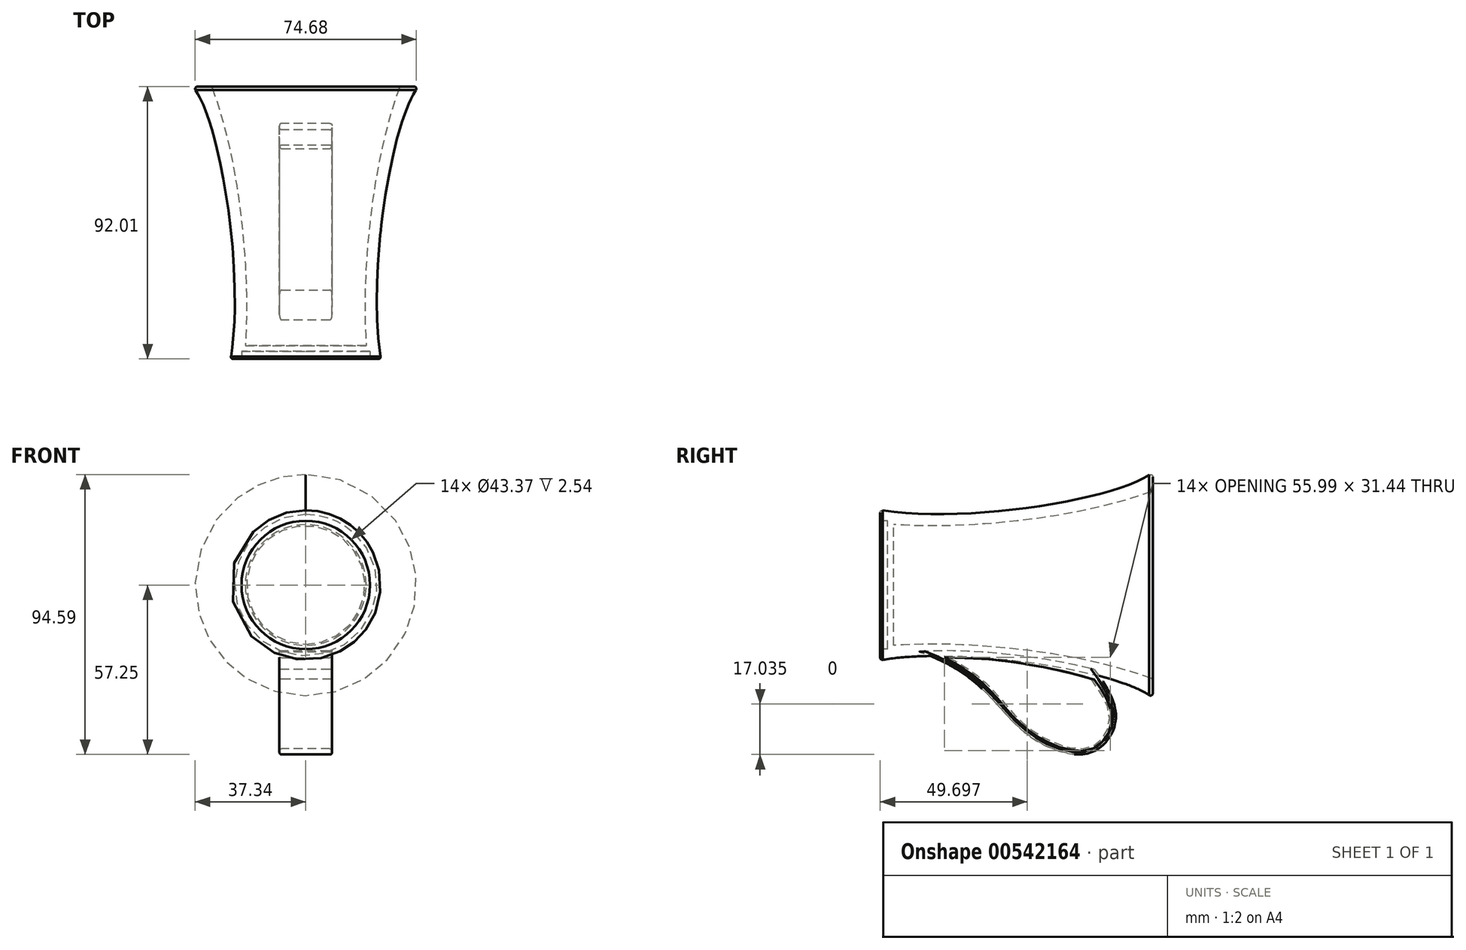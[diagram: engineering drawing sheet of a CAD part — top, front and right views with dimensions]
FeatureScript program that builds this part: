
annotation { "Feature Type Name" : "Feature", "Feature Type Description" : "" }
export const myFeature = defineFeature(function(context is Context, id is Id, definition is map)
    precondition{}
    {
        {
            var Q0;
            Q0=qCreatedBy(makeId("Top.planeOp"),FACE);
            var sketch = newSketch(context, id + "F0", { "sketchPlane" : qUnion([Q0])});
            skLineSegment(sketch, "E0", {"start": v(0, -41.4) * mm, "end": v(25.4, -41.4) * mm});
            skLineSegment(sketch, "E1", {"start": v(0, 50.6) * mm, "end": v(38.1, 50.6) * mm});
            skFitSpline(sketch, "E2", {"points": [v(38.1, 50.6) * mm, v(25.4, -41.4) * mm], "startDerivative": vector(-27.2, -32.14) * mm, "endDerivative": vector(14.87, -86.25) * mm});
            skLineSegment(sketch, "E3", {"start": v(0, 50.6) * mm, "end": v(0, -41.4) * mm});
            skSolve(sketch);
        }
        {
            var Q0;
            Q0 = qSketchRegion(id + "F0", true);
            var Q1;
            Q1=sQuery(id+"F0.wireOp",EDGE,"E3");
            revolve(context, id + "F1", {"entities" : qUnion([Q0]), "axis" : qUnion([Q1]), "revolveType" : RevolveType.FULL});
        }
        {
            var Q0;
            Q0=qCreatedBy(makeId("Top.planeOp"),FACE);
            var sketch = newSketch(context, id + "F2", { "sketchPlane" : qUnion([Q0])});
            skLineSegment(sketch, "E4", {"start": v(0, -36.85) * mm, "end": v(20.4, -36.85) * mm});
            skLineSegment(sketch, "E5", {"start": v(0, 55.37) * mm, "end": v(33.64, 55.37) * mm});
            skFitSpline(sketch, "E6", {"points": [v(33.64, 55.37) * mm, v(21.16, 0) * mm, v(20.4, -36.85) * mm], "startDerivative": vector(-40.95, -98.28) * mm, "endDerivative": vector(5.08, -78.76) * mm});
            skLineSegment(sketch, "E7", {"start": v(0, 55.37) * mm, "end": v(0, -36.85) * mm});
            skSolve(sketch);
        }
        {
            var Q0;
            Q0=makeQuery(id+"F2.imprint","IMPRINT",FACE,{"disambiguationData":[TD([[makeQuery(id+"F2.imprint","IMPRINT",EDGE,{"derivedFrom":sQuery(id+"F2.wireOp",EDGE,"E4")}),1.0]])]});
            var Q1;
            Q1=sQuery(id+"F2.wireOp",EDGE,"E7");
            revolve(context, id + "F3", {"operationType" : NewBodyOperationType.REMOVE, "entities" : qUnion([Q0]), "axis" : qUnion([Q1]), "revolveType" : RevolveType.FULL, "oppositeDirection" : true});
        }
        {
            var Q0;
            Q0=qCreatedBy(makeId("Right.planeOp"),FACE);
            var sketch = newSketch(context, id + "F4", { "sketchPlane" : qUnion([Q0])});
            skFitSpline(sketch, "E8", {"points": [v(30.84, -28.48) * mm, v(37.82, -47.26) * mm, v(29, -56.82) * mm, v(8.9, -50.94) * mm, v(-7.03, -35) * mm, v(-28.21, -22.6) * mm], "startDerivative": vector(93.3, -124.4) * mm, "endDerivative": vector(-113.4, 37.53) * mm});
            skFitSpline(sketch, "E9", {"points": [v(30.84, -28.48) * mm, v(0, -23.26) * mm, v(-28.21, -22.6) * mm], "startDerivative": vector(-67.42, 16.21) * mm, "endDerivative": vector(-57.3, -5) * mm});
            skSolve(sketch);
        }
        {
            var Q0;
            Q0 = qSketchRegion(id + "F4", true);
            extrude(context, id + "F5", {"entities" : qUnion([Q0]), "endBound" : BoundingType.SYMMETRIC, "depth" : 17.78 * mm, "offsetDistance" : 25.4 * mm});
        }
        {
            var Q0;
            Q0=makeQuery(id+"F5.opExtrude","CAP_FACE",FACE,{"disambiguationData":[OSD([sQuery(id+"F4.wireOp",EDGE,"E8"),sQuery(id+"F4.wireOp",EDGE,"E9")])],"isStart":false});
            var sketch = newSketch(context, id + "F6", { "sketchPlane" : qUnion([Q0])});
            skFitSpline(sketch, "E10", {"points": [v(29.68, -31.62) * mm, v(8.76, -26.89) * mm, v(-18.07, -24.52) * mm], "startDerivative": vector(-65.8, 18.8) * mm, "endDerivative": vector(-81.13, 1.2) * mm});
            skFitSpline(sketch, "E11", {"points": [v(29.68, -31.62) * mm, v(36, -44.25) * mm, v(29.68, -54.7) * mm, v(10.34, -49.38) * mm, v(-1.5, -37.54) * mm, v(-18.07, -24.52) * mm], "startDerivative": vector(41.3, -59.3) * mm, "endDerivative": vector(-115.82, 63.17) * mm});
            skSolve(sketch);
        }
        {
            var Q0;
            Q0=makeQuery(id+"F6.imprint","IMPRINT",FACE,{"disambiguationData":[TD([[makeQuery(id+"F6.imprint","IMPRINT",EDGE,{"derivedFrom":sQuery(id+"F6.wireOp",EDGE,"E10")}),1.0]])]});
            extrude(context, id + "F7", {"entities" : qUnion([Q0]), "operationType" : NewBodyOperationType.REMOVE, "endBound" : BoundingType.SYMMETRIC, "oppositeDirection" : true, "depth" : 43.69 * mm, "offsetDistance" : 25.4 * mm});
        }
        {
            var Q0;
            Q0=makeQuery(id+"F1.opRevolve","SWEPT_FACE",FACE,{"disambiguationData":[OSD([sQuery(id+"F0.wireOp",EDGE,"E0")])]});
            var sketch = newSketch(context, id + "F8", { "sketchPlane" : qUnion([Q0])});
            skCircle(sketch, "E12", {"center": v(0, 0) * mm, "radius": 21.69 * mm});
            skSolve(sketch);
        }
        {
            var Q0;
            Q0=makeQuery(id+"F8.imprint","IMPRINT",FACE,{"disambiguationData":[TD([[makeQuery(id+"F8.imprint","IMPRINT",EDGE,{"derivedFrom":sQuery(id+"F8.wireOp",EDGE,"E12")}),1.0]])]});
            extrude(context, id + "F9", {"entities" : qUnion([Q0]), "operationType" : NewBodyOperationType.REMOVE, "oppositeDirection" : true, "depth" : 2.54 * mm, "offsetDistance" : 25.4 * mm});
        }
        {
            var Q0;
            Q0=makeQuery(id+"F1.opRevolve","SWEPT_EDGE",EDGE,{"disambiguationData":[OSD([sQuery(id+"F0.wireOp",EDGE,"E0"),sQuery(id+"F0.wireOp",EDGE,"E2")])]});
            var Q1;
            Q1=makeQuery(id+"F9.boolean.opBoolean","COPY",EDGE,{"derivedFrom":makeQuery(id+"F9.opExtrude","CAP_EDGE",EDGE,{"disambiguationData":[OSD([sQuery(id+"F8.wireOp",EDGE,"E12")])],"isStart":true})});
            var Q2;
            Q2=makeQuery(id+"F5.opExtrude","CAP_EDGE",EDGE,{"disambiguationData":[OSD([sQuery(id+"F4.wireOp",EDGE,"E8")])],"isStart":true});
            var Q3;
            Q3=makeQuery(id+"F7.boolean.opBoolean","INTERSECT",EDGE,{"derivedFrom":[makeQuery(id+"F5.opExtrude","CAP_FACE",FACE,{"disambiguationData":[OSD([sQuery(id+"F4.wireOp",EDGE,"E8"),sQuery(id+"F4.wireOp",EDGE,"E9")])],"isStart":true}),makeQuery(id+"F7.opExtrude","SWEPT_FACE",FACE,{"disambiguationData":[OSD([sQuery(id+"F6.wireOp",EDGE,"E11")])]})]});
            var Q4;
            Q4=makeQuery(id+"F5.opExtrude","CAP_EDGE",EDGE,{"disambiguationData":[OSD([sQuery(id+"F4.wireOp",EDGE,"E8")])],"isStart":false});
            var Q5;
            Q5=makeQuery(id+"F7.boolean.opBoolean","INTERSECT",EDGE,{"derivedFrom":[makeQuery(id+"F5.opExtrude","CAP_FACE",FACE,{"disambiguationData":[OSD([sQuery(id+"F4.wireOp",EDGE,"E8"),sQuery(id+"F4.wireOp",EDGE,"E9")])],"isStart":false}),makeQuery(id+"F7.opExtrude","SWEPT_FACE",FACE,{"disambiguationData":[OSD([sQuery(id+"F6.wireOp",EDGE,"E11")])]})]});
            var Q6;
            Q6=makeQuery(id+"F1.opRevolve","SWEPT_EDGE",EDGE,{"disambiguationData":[OSD([sQuery(id+"F0.wireOp",EDGE,"E1"),sQuery(id+"F0.wireOp",EDGE,"E2")])]});
            var Q7;
            Q7=makeQuery(id+"F3.boolean.opBoolean","INTERSECT",EDGE,{"derivedFrom":[makeQuery(id+"F1.opRevolve","SWEPT_FACE",FACE,{"disambiguationData":[OSD([sQuery(id+"F0.wireOp",EDGE,"E1")])]}),makeQuery(id+"F3.opRevolve","SWEPT_FACE",FACE,{"disambiguationData":[OSD([sQuery(id+"F2.wireOp",EDGE,"E6")])]})]});
            fillet(context, id + "F10", {"entities" : qUnion([Q0, Q1, Q2, Q3, Q4, Q5, Q6, Q7]), "radius" : 0.76 * mm, "tangentPropagation" : true, "allowEdgeOverflow" : false});
        }
    });
